# Revit family: BOILER_RMAX_R600EVO_601-603
name_source: partatom
category: Generic Models
revit_build: Autodesk Revit 2014 (Build: 20130308_1515(x64)
units: mm (PartAtom-declared; Revit-internal decimal feet)

## types (3) — shared parameters
Air_ConnectionDia = 130 mm
Air_SpigotDia = 135 mm  [stored 0.442913 ft]
Assembly Code = D3020100
Condensate_ConnectionDia = 32 mm
Condensate_SpigotDia = 42 mm  [stored 0.137795 ft]
ControlPanel_Depth = 160 mm  [stored 0.524934 ft]
ControlPanel_Height = 159 mm  [stored 0.521654 ft]
Density_Water_70 = 977.8000 kg/m³
Equipment_Fuel = Natural Gas (G20)
Equipment_Height = 1470 mm
Equipment_Power_Factor = 0.9
Equipment_Width = 466 mm  [stored 1.52887 ft]
Flue_GasTemp = 90 °C
Flue_SpigotDia = 260 mm  [stored 0.853018 ft]
Frequency = 50 Hz
Gas_ConnectionDia = 40 mm
Gas_SpigotDia = 48 mm  [stored 0.15748 ft]
HTGF_ConnectionDia = 50 mm
HTGF_SpigotDia = 60 mm  [stored 0.19685 ft]
HTGR_ConnectionDia = 50 mm
HTGR_SpigotDia = 60 mm  [stored 0.19685 ft]
Issue_Date = 07-09-2017
Issue_Rev = A
Manufacturer = Rendamax
Maximum_Overcurrent_Protection = 16 A
Panel_Width = 339 mm  [stored 1.1122 ft]
Phase = 3
Seasonal_Energy_Efficiency = 98.2
Specific_Heat_Water = 4.2000 J/(g·°C)
UnitConvert_Area = 1 m²
Voltage = 400 V

## per-type parameters (varying)
| type | Boiler_Nominal_Output_40_30 | Boiler_Nominal_Output_80_60 | Equipment_Apparent_Power | Equipment_Depth | Equipment_Fuel_Flow | Equipment_Rated_Power | Flue_ConnectionDia | Model | UnitConvert_PressureFactor | Water_Content_HTG | Weight_Dry | Weight_Operating |
| R601 | 151 kW | 142 kW | 196 VA | 1165 mm | 13.3 m3/hr | 176 W | 150 mm | R600 EVO 601 | 3816074 | 26.0 L | 290.00 kg | 316.00 kg |
| R602 | 202 kW | 190 kW | 297 VA | 1315 mm | 17.8 m3/hr | 267 W | 150 mm | R600 EVO 602 | 5100462 | 31.0 L | 332.00 kg | 363.00 kg |
| R603 | 252 kW | 238 kW | 318 VA | 1465 mm  [stored 4.80643 ft] | 22.2 m3/hr | 286 W | 200 mm | R600 EVO 603 | 3813031 | 33.0 L | 366.00 kg | 399.00 kg |

note: column(s) folded — value = type name in every type: Type Comments

note: [stored X ft] marks values corroborated as IEEE doubles in the binary element streams (Revit-internal decimal feet)

## geometry (parser evidence)
native form markers: Sweep x6
no freeform markers — native parametric forms only
